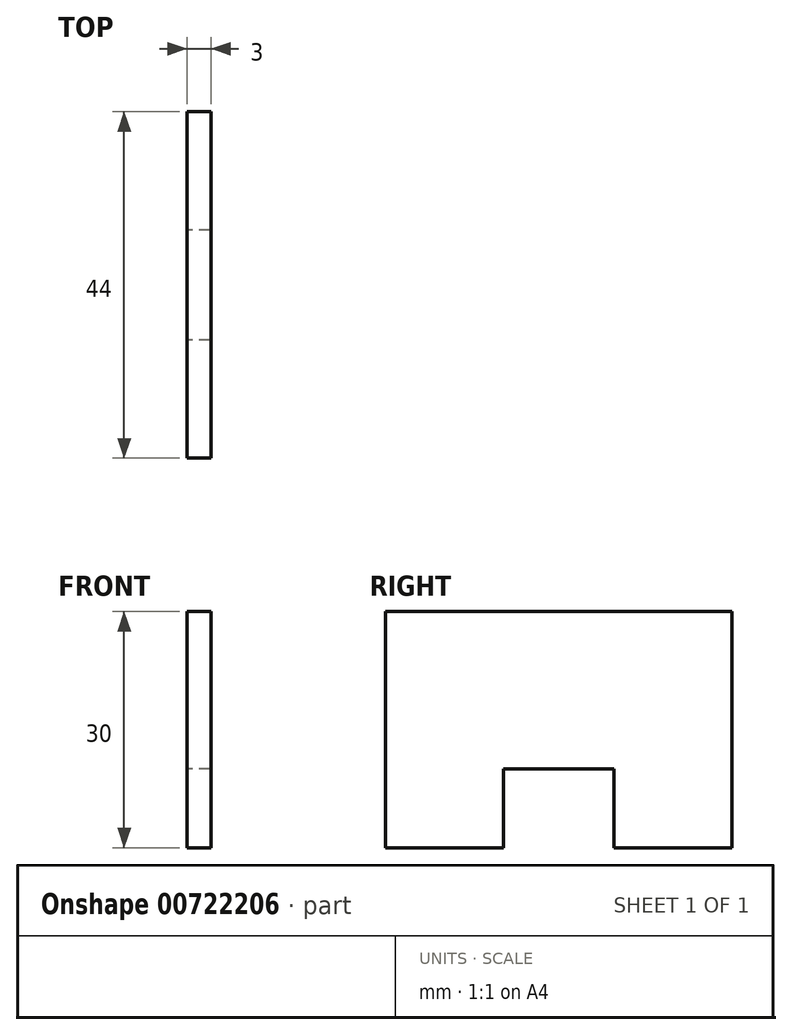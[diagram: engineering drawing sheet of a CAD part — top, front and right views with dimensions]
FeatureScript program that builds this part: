
annotation { "Feature Type Name" : "Feature", "Feature Type Description" : "" }
export const myFeature = defineFeature(function(context is Context, id is Id, definition is map)
    precondition{}
    {
        {
            var Q0;
            Q0=qCreatedBy(makeId("Right.planeOp"),FACE);
            var sketch = newSketch(context, id + "F0", { "sketchPlane" : qUnion([Q0])});
            skLineSegment(sketch, "E0.bottom", {"start": v(30.8, 17.16) * mm, "end": v(74.8, 17.16) * mm});
            skLineSegment(sketch, "E0.top", {"start": v(30.8, -12.84) * mm, "end": v(45.8, -12.84) * mm});
            skLineSegment(sketch, "E0.left", {"start": v(30.8, 17.16) * mm, "end": v(30.8, -12.84) * mm});
            skLineSegment(sketch, "E0.right", {"start": v(74.8, 17.16) * mm, "end": v(74.8, -12.84) * mm});
            skLineSegment(sketch, "E1", {"start": v(45.8, -12.84) * mm, "end": v(30.8, -12.84) * mm});
            skLineSegment(sketch, "E2", {"start": v(45.8, -12.84) * mm, "end": v(45.8, -2.84) * mm});
            skLineSegment(sketch, "E3", {"start": v(45.8, -2.84) * mm, "end": v(59.8, -2.84) * mm});
            skLineSegment(sketch, "E4", {"start": v(59.8, -2.84) * mm, "end": v(59.8, -12.84) * mm});
            skLineSegment(sketch, "E5.trimOffspring", {"start": v(59.8, -12.84) * mm, "end": v(74.8, -12.84) * mm});
            skPoint(sketch, "E6.start.orphan", {"position": v(52.8, -12.84) * mm});
            skSolve(sketch);
        }
        {
            var Q0;
            Q0=makeQuery(id+"F0.imprint","IMPRINT",FACE,{"disambiguationData":[TD([[makeQuery(id+"F0.imprint","IMPRINT",EDGE,{"derivedFrom":sQuery(id+"F0.wireOp",EDGE,"E0.bottom")}),-1.0]])]});
            extrude(context, id + "F1", {"entities" : qUnion([Q0]), "depth" : 3 * mm, "offsetDistance" : 25 * mm});
        }
    });
